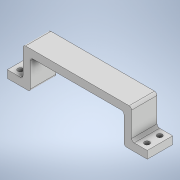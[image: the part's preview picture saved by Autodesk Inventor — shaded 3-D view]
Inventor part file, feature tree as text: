
AUTODESK INVENTOR PART (.ipt)
format: ipt  version: 2022 (Build 260153000, 153)  size: 141,312 bytes
history: native  units: mm
features: extrude x2, sketch x2, mirror x1
ambient origin geometry x8: Origin, YZ Plane, XZ Plane, XY Plane, X Axis, Y Axis, Z Axis, Center Point
bodies: Solid1 (feature_tree)
feature tree (5):
  extrude  "Extrusion1"  Depth=6.0mm
  extrude  "Extrusion2"  Depth=2.0mm
  mirror  "Mirror1"
  sketch  "Sketch1"  dims[d0=6.0mm d1=6.0mm]
  sketch  "Sketch2"  dims[d2=6.0mm d3=2.0mm d4=20.0mm d5=0.0mm d7=10.0mm d8=5.0mm d9=4.0mm d10=4.0mm d11=20.0mm d12=0.0mm]
